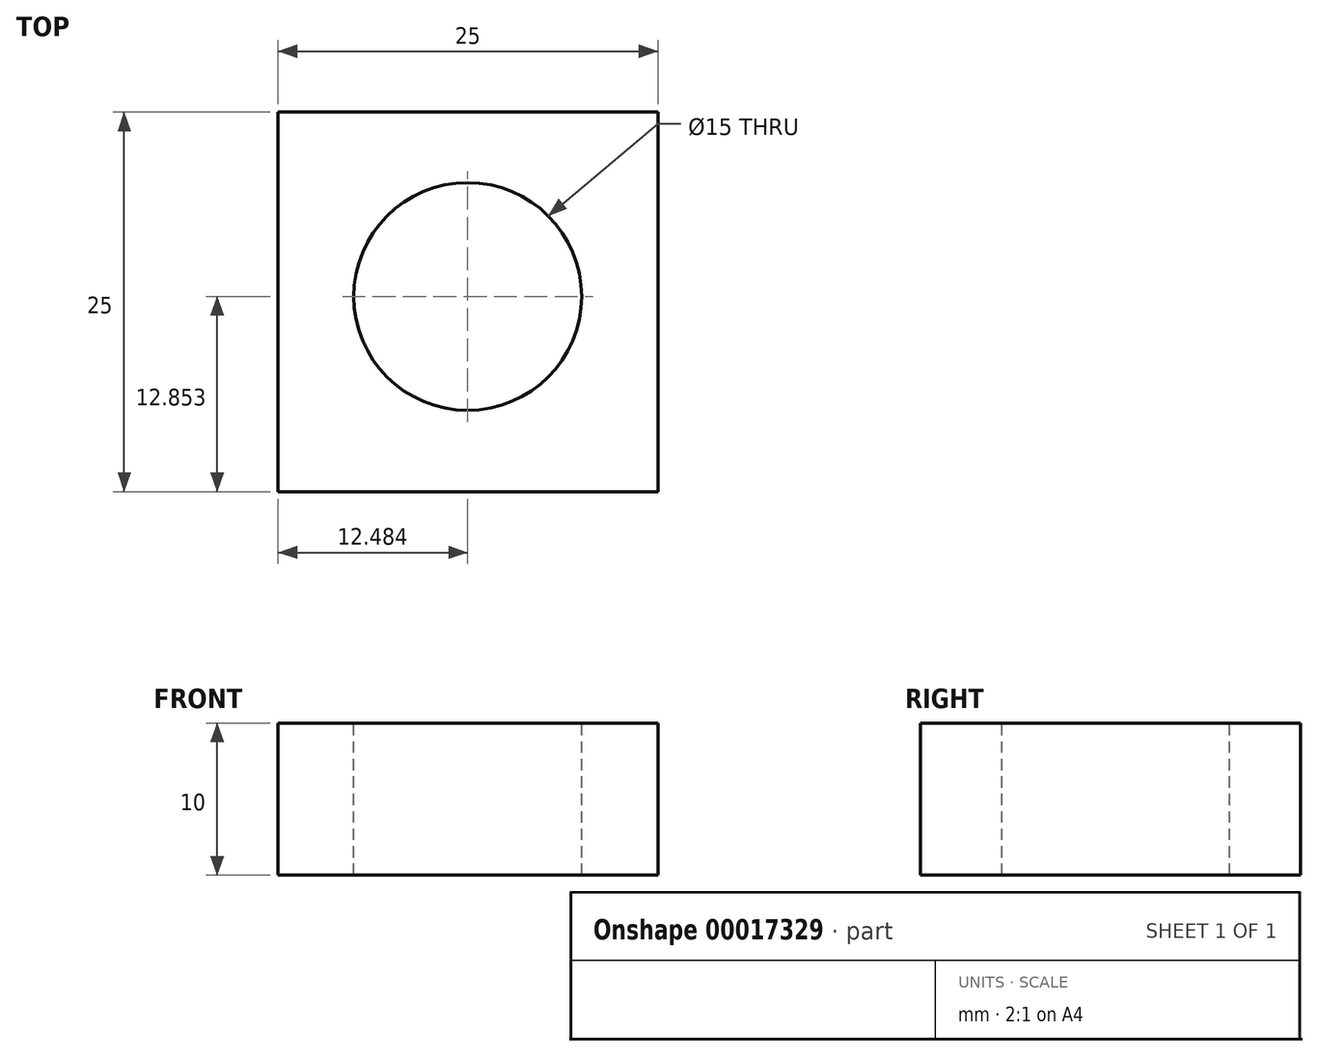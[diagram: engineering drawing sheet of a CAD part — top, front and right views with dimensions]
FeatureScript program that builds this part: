
annotation { "Feature Type Name" : "Feature", "Feature Type Description" : "" }
export const myFeature = defineFeature(function(context is Context, id is Id, definition is map)
    precondition{}
    {
        {
            var Q0;
            Q0=qCreatedBy(makeId("Front.planeOp"),FACE);
            var sketch = newSketch(context, id + "F0", { "sketchPlane" : qUnion([Q0])});
            skLineSegment(sketch, "E0", {"start": v(-8.62, -5) * mm, "end": v(-8.62, 5) * mm});
            skLineSegment(sketch, "E1", {"start": v(-8.62, 5) * mm, "end": v(16.38, 5) * mm});
            skLineSegment(sketch, "E2", {"start": v(16.38, 5) * mm, "end": v(16.38, -5) * mm});
            skLineSegment(sketch, "E3", {"start": v(16.38, -5) * mm, "end": v(-8.62, -5) * mm});
            skSolve(sketch);
        }
        {
            var Q0;
            Q0 = qSketchRegion(id + "F0", true);
            extrude(context, id + "F1", {"entities" : qUnion([Q0]), "depth" : 25 * mm});
        }
        {
            var Q0;
            Q0=makeQuery(id+"F1.opExtrude","SWEPT_FACE",FACE,{"disambiguationData":[OSD([sQuery(id+"F0.wireOp",EDGE,"E1")])]});
            var sketch = newSketch(context, id + "F2", { "sketchPlane" : qUnion([Q0])});
            skLineSegment(sketch, "E4", {"start": v(3.88, 0) * mm, "end": v(3.88, -25) * mm});
            skSolve(sketch);
        }
        {
            var Q0;
            {var subQ2=sQuery(id+"F2.wireOp",EDGE,"E4");Q0=makeQuery(id+"F2.imprint","IMPRINT",FACE,{"disambiguationData":[TD([[makeQuery(id+"F2.imprint","IMPRINT",EDGE,{"derivedFrom":subQ2}),-1.0]])]});}
            var sketch = newSketch(context, id + "F3", { "sketchPlane" : qUnion([Q0])});
            skCircle(sketch, "E5", {"center": v(3.86, -12.15) * mm, "radius": 8.4 * mm});
            skSolve(sketch);
        }
        {
            var Q0;
            Q0=sQuery(id+"F3.wireOp",VERTEX,"E5.center");
            var Q1;
            Q1=makeQuery(id+"F1.opExtrude","SWEPT_BODY",BODY,{"disambiguationData":[OSD([sQuery(id+"F0.wireOp",EDGE,"E0"),sQuery(id+"F0.wireOp",EDGE,"E1"),sQuery(id+"F0.wireOp",EDGE,"E2"),sQuery(id+"F0.wireOp",EDGE,"E3")])]});
            hole(context, id + "F4", {"style" : HoleStyle.SIMPLE, "holeDiameter" : 15 * mm, "endStyle" : HoleEndStyle.THROUGH, "locations" : qUnion([Q0]), "scope" : qUnion([Q1])});
        }
    });
